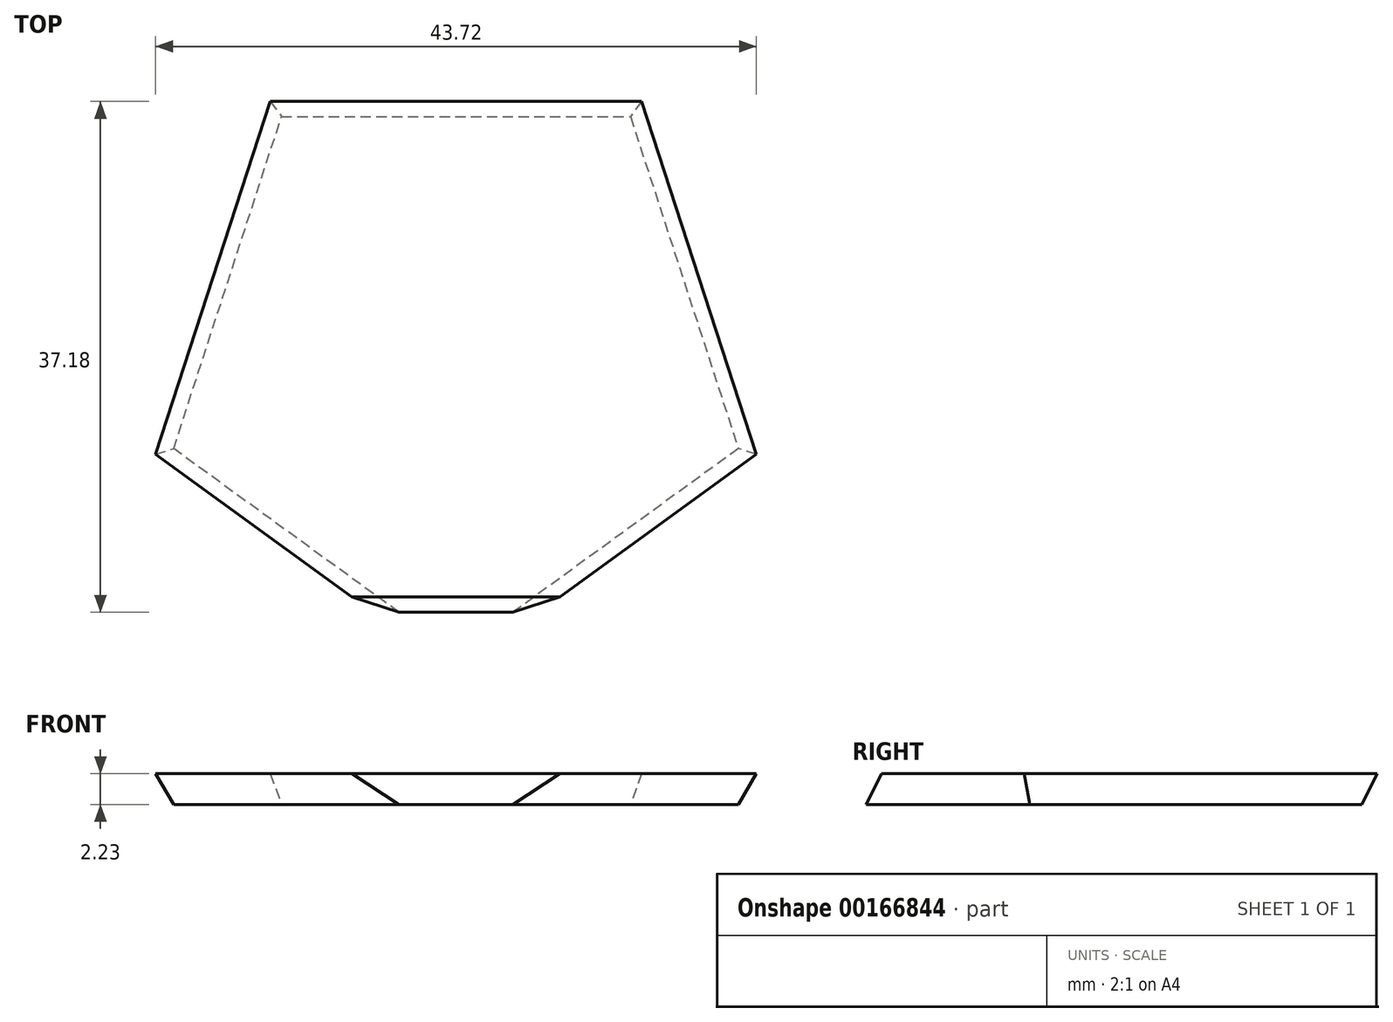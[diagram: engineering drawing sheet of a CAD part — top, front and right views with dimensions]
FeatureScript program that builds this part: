
annotation { "Feature Type Name" : "Feature", "Feature Type Description" : "" }
export const myFeature = defineFeature(function(context is Context, id is Id, definition is map)
    precondition{}
    {
        {
            var Q0;
            Q0=qCreatedBy(makeId("Top.planeOp"),FACE);
            var sketch = newSketch(context, id + "F0", { "sketchPlane" : qUnion([Q0])});
            skCircle(sketch, "E0.cCircle", {"center": v(0, 0) * mm, "radius": 17.48 * mm, "construction": true});
            skLineSegment(sketch, "E0.0", {"start": v(-12.7, 17.48) * mm, "end": v(12.7, 17.48) * mm});
            skLineSegment(sketch, "E0.1", {"start": v(12.7, 17.48) * mm, "end": v(20.55, -6.68) * mm});
            skLineSegment(sketch, "E0.2", {"start": v(20.55, -6.68) * mm, "end": v(0, -21.6) * mm});
            skLineSegment(sketch, "E0.3", {"start": v(0, -21.6) * mm, "end": v(-20.55, -6.68) * mm});
            skLineSegment(sketch, "E0.4", {"start": v(-20.55, -6.68) * mm, "end": v(-12.7, 17.48) * mm});
            skPoint(sketch, "E0.0.midPoint", {"position": v(0, 17.48) * mm});
            skSolve(sketch);
        }
        {
            var Q0;
            Q0=makeQuery(id+"F0.imprint","IMPRINT",FACE,{"disambiguationData":[TD([[makeQuery(id+"F0.imprint","IMPRINT",EDGE,{"derivedFrom":sQuery(id+"F0.wireOp",EDGE,"E0.0")}),-1.0]])]});
            extrude(context, id + "F1", {"entities" : qUnion([Q0]), "depth" : ((1 / sin(36 * degree)) * (sin(18 * degree) + 1)) * mm, "hasDraft" : true, "draftAngle" : acos(-1 / sqrt(5)) - 90 * degree});
        }
        {
            var Q0;
            Q0=makeQuery(id+"F1.opExtrude","CAP_FACE",FACE,{"disambiguationData":[OSD([sQuery(id+"F0.wireOp",EDGE,"E0.0"),sQuery(id+"F0.wireOp",EDGE,"E0.1"),sQuery(id+"F0.wireOp",EDGE,"E0.2"),sQuery(id+"F0.wireOp",EDGE,"E0.3"),sQuery(id+"F0.wireOp",EDGE,"E0.4")])],"isStart":false});
            var sketch = newSketch(context, id + "F2", { "sketchPlane" : qUnion([Q0])});
            skCircle(sketch, "E1.cCircle", {"center": v(0, 0) * mm, "radius": 17.48 * mm, "construction": true});
            skLineSegment(sketch, "E1.0", {"start": v(12.7, -17.48) * mm, "end": v(-12.7, -17.48) * mm});
            skLineSegment(sketch, "E1.1", {"start": v(-12.7, -17.48) * mm, "end": v(-20.55, 6.68) * mm});
            skLineSegment(sketch, "E1.2", {"start": v(-20.55, 6.68) * mm, "end": v(0, 21.6) * mm});
            skLineSegment(sketch, "E1.3", {"start": v(0, 21.6) * mm, "end": v(20.55, 6.68) * mm});
            skLineSegment(sketch, "E1.4", {"start": v(20.55, 6.68) * mm, "end": v(12.7, -17.48) * mm});
            skPoint(sketch, "E1.0.midPoint", {"position": v(0, -17.48) * mm});
            skSolve(sketch);
        }
        {
            var Q0;
            Q0=makeQuery(id+"F2.imprint","IMPRINT",FACE,{"disambiguationData":[TD([[makeQuery(id+"F2.imprint","IMPRINT",EDGE,{"derivedFrom":sQuery(id+"F2.wireOp",EDGE,"E1.0")}),1.0]])]});
            extrude(context, id + "F3", {"entities" : qUnion([Q0]), "operationType" : NewBodyOperationType.REMOVE, "endBound" : BoundingType.THROUGH_ALL, "oppositeDirection" : true, "depth" : 25.4 * mm, "hasDraft" : true, "draftAngle" : acos(-1 / sqrt(5)) - 90 * degree, "draftPullDirection" : true});
        }
    });
